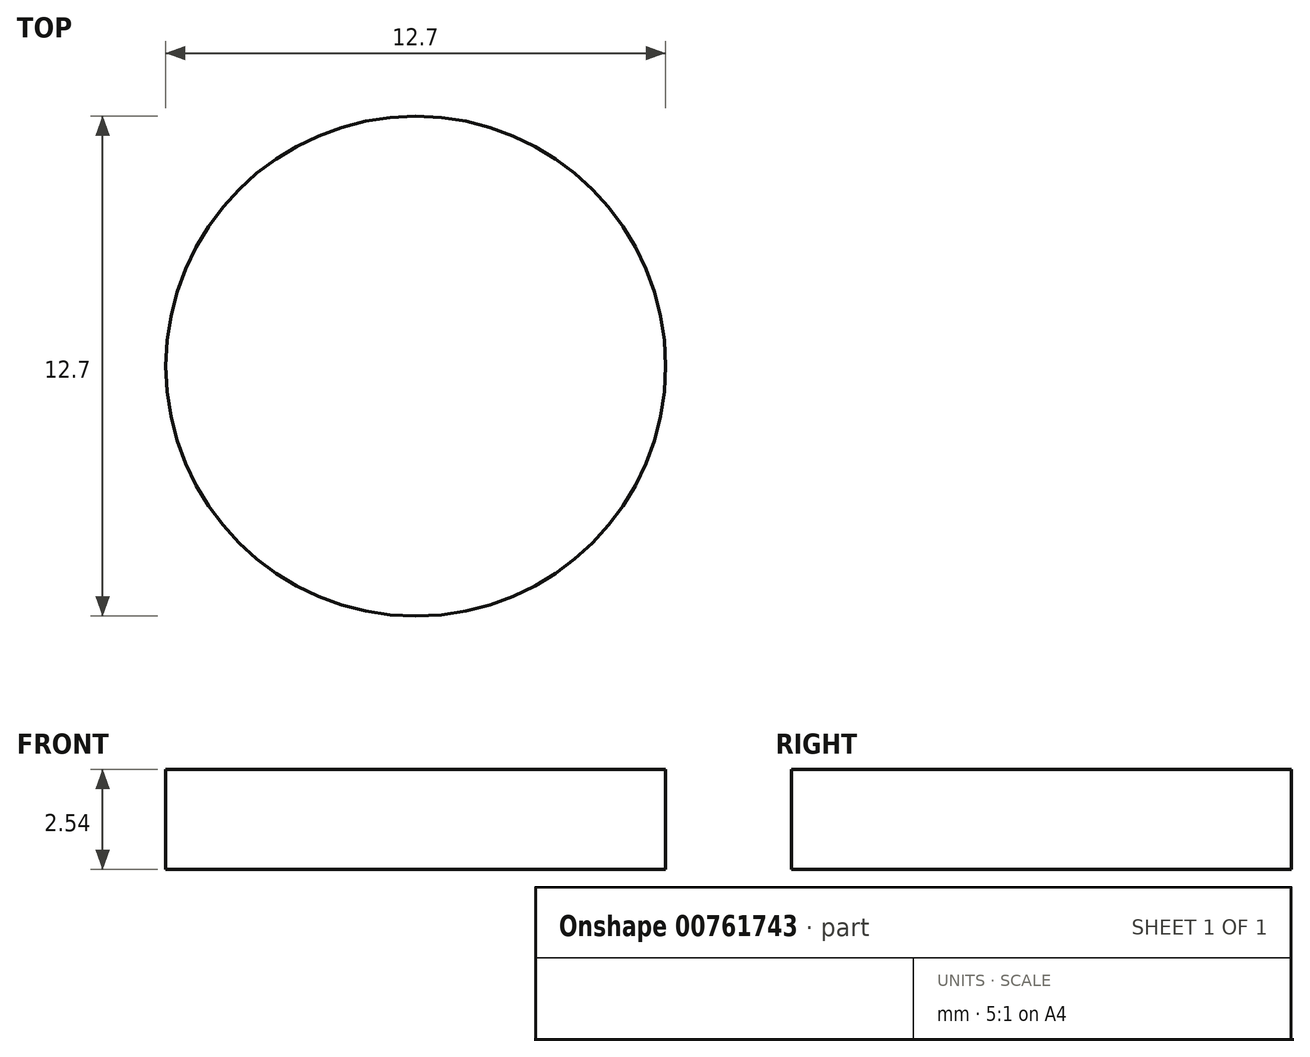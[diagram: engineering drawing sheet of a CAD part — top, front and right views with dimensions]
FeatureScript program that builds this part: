
annotation { "Feature Type Name" : "Feature", "Feature Type Description" : "" }
export const myFeature = defineFeature(function(context is Context, id is Id, definition is map)
    precondition{}
    {
        {
            var Q0;
            Q0=qCreatedBy(makeId("Top.planeOp"),FACE);
            var sketch = newSketch(context, id + "F0", { "sketchPlane" : qUnion([Q0])});
            skCircle(sketch, "E0", {"center": v(-39.9, 27.37) * mm, "radius": 6.35 * mm});
            skSolve(sketch);
        }
        {
            var Q0;
            Q0=makeQuery(id+"F0.imprint","IMPRINT",FACE,{"disambiguationData":[TD([[makeQuery(id+"F0.imprint","IMPRINT",EDGE,{"derivedFrom":sQuery(id+"F0.wireOp",EDGE,"E0")}),1.0]])]});
            extrude(context, id + "F1", {"entities" : qUnion([Q0]), "depth" : 2.54 * mm, "offsetDistance" : 25.4 * mm});
        }
    });
